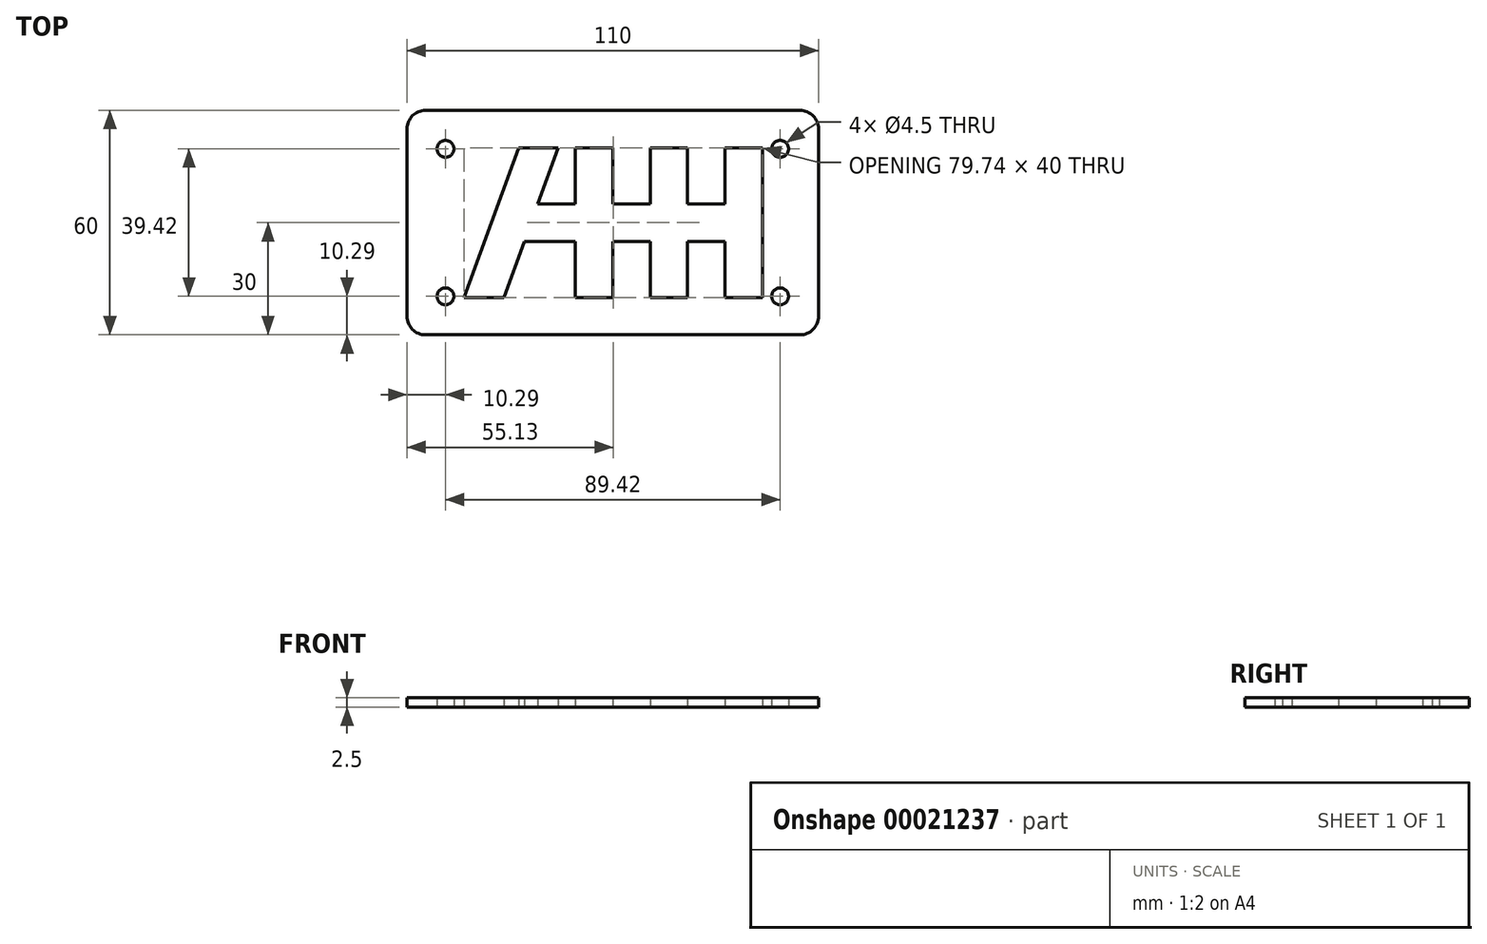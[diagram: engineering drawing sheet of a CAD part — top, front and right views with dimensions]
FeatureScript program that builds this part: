
annotation { "Feature Type Name" : "Feature", "Feature Type Description" : "" }
export const myFeature = defineFeature(function(context is Context, id is Id, definition is map)
    precondition{}
    {
        {
            var Q0;
            Q0=qCreatedBy(makeId("Top.planeOp"),FACE);
            var sketch = newSketch(context, id + "F0", { "sketchPlane" : qUnion([Q0])});
            skLineSegment(sketch, "E0.rect.bottom", {"start": v(50, -30) * mm, "end": v(-50, -30) * mm});
            skLineSegment(sketch, "E0.rect.top", {"start": v(50, 30) * mm, "end": v(-50, 30) * mm});
            skLineSegment(sketch, "E0.rect.left", {"start": v(55, -25) * mm, "end": v(55, 25) * mm});
            skLineSegment(sketch, "E0.rect.right", {"start": v(-55, -25) * mm, "end": v(-55, 25) * mm});
            skPoint(sketch, "E0.rect.middle", {"position": v(0, 0) * mm});
            skPoint(sketch, "E1.visualSharp", {"position": v(-55, 30) * mm});
            skArc(sketch, "E1.filletArc", {"start": v(-50, 30) * mm, "mid": v(-53.54, 28.54) * mm, "end": v(-55, 25) * mm});
            skPoint(sketch, "E2.visualSharp", {"position": v(55, 30) * mm});
            skArc(sketch, "E2.filletArc", {"start": v(55, 25) * mm, "mid": v(53.54, 28.54) * mm, "end": v(50, 30) * mm});
            skPoint(sketch, "E3.visualSharp", {"position": v(55, -30) * mm});
            skArc(sketch, "E3.filletArc", {"start": v(50, -30) * mm, "mid": v(53.54, -28.54) * mm, "end": v(55, -25) * mm});
            skPoint(sketch, "E4.visualSharp", {"position": v(-55, -30) * mm});
            skArc(sketch, "E4.filletArc", {"start": v(-55, -25) * mm, "mid": v(-53.54, -28.54) * mm, "end": v(-50, -30) * mm});
            skLineSegment(sketch, "E5", {"start": v(0, 30) * mm, "end": v(0, -30) * mm, "construction": true});
            skLineSegment(sketch, "E6", {"start": v(-55, 0) * mm, "end": v(55, 0) * mm, "construction": true});
            skCircle(sketch, "E7", {"center": v(-44.7, 19.7) * mm, "radius": 2.25 * mm});
            skCircle(sketch, "E8.MirrorC", {"center": v(44.7, 19.7) * mm, "radius": 2.25 * mm});
            skCircle(sketch, "E9.MirrorC", {"center": v(-44.7, -19.7) * mm, "radius": 2.25 * mm});
            skCircle(sketch, "E10.MirrorC", {"center": v(44.7, -19.7) * mm, "radius": 2.25 * mm});
            skLineSegment(sketch, "E11", {"start": v(-10, 20) * mm, "end": v(0, 20) * mm});
            skLineSegment(sketch, "E12", {"start": v(0, 20) * mm, "end": v(0, 5) * mm});
            skLineSegment(sketch, "E13", {"start": v(0, 5) * mm, "end": v(10, 5) * mm});
            skLineSegment(sketch, "E14", {"start": v(10, 5) * mm, "end": v(10, 20) * mm});
            skLineSegment(sketch, "E15", {"start": v(10, 20) * mm, "end": v(20, 20) * mm});
            skLineSegment(sketch, "E16", {"start": v(20, 20) * mm, "end": v(20, 5) * mm});
            skLineSegment(sketch, "E17", {"start": v(20, 5) * mm, "end": v(30, 5) * mm});
            skLineSegment(sketch, "E18", {"start": v(30, 5) * mm, "end": v(30, 20) * mm});
            skLineSegment(sketch, "E19", {"start": v(30, 20) * mm, "end": v(40, 20) * mm});
            skLineSegment(sketch, "E20", {"start": v(40, 20) * mm, "end": v(40, -20) * mm});
            skLineSegment(sketch, "E21", {"start": v(40, -20) * mm, "end": v(30, -20) * mm});
            skLineSegment(sketch, "E22", {"start": v(30, -20) * mm, "end": v(30, -5) * mm});
            skLineSegment(sketch, "E23", {"start": v(30, -5) * mm, "end": v(20, -5) * mm});
            skLineSegment(sketch, "E24", {"start": v(20, -5) * mm, "end": v(20, -20) * mm});
            skLineSegment(sketch, "E25", {"start": v(20, -20) * mm, "end": v(10, -20) * mm});
            skLineSegment(sketch, "E26", {"start": v(10, -20) * mm, "end": v(10, -5) * mm});
            skLineSegment(sketch, "E27", {"start": v(10, -5) * mm, "end": v(0, -5) * mm});
            skLineSegment(sketch, "E28", {"start": v(0, -5) * mm, "end": v(0, -20) * mm});
            skLineSegment(sketch, "E29", {"start": v(0, -20) * mm, "end": v(-10, -20) * mm});
            skLineSegment(sketch, "E30", {"start": v(-25.18, 20) * mm, "end": v(-39.74, -20) * mm});
            skLineSegment(sketch, "E31", {"start": v(-39.74, -20) * mm, "end": v(-29.1, -20) * mm});
            skLineSegment(sketch, "E32", {"start": v(-29.1, -20) * mm, "end": v(-23.64, -5) * mm});
            skLineSegment(sketch, "E33", {"start": v(-23.64, -5) * mm, "end": v(-10, -5) * mm});
            skLineSegment(sketch, "E34", {"start": v(-10, -5) * mm, "end": v(-10, -20) * mm});
            skLineSegment(sketch, "E35", {"start": v(-10, 20) * mm, "end": v(-10, 5) * mm});
            skLineSegment(sketch, "E36", {"start": v(-10, 5) * mm, "end": v(-20, 5) * mm});
            skLineSegment(sketch, "E37", {"start": v(-20, 5) * mm, "end": v(-14.54, 20) * mm});
            skLineSegment(sketch, "E38", {"start": v(-14.54, 20) * mm, "end": v(-25.18, 20) * mm});
            skLineSegment(sketch, "E39", {"start": v(-20, 5) * mm, "end": v(-29.4, 8.42) * mm, "construction": true});
            skLineSegment(sketch, "E40", {"start": v(-29.1, -20) * mm, "end": v(-14.54, 20) * mm, "construction": true});
            skLineSegment(sketch, "E41", {"start": v(0, 5) * mm, "end": v(0, -5) * mm, "construction": true});
            skLineSegment(sketch, "E42", {"start": v(-44.7, -19.7) * mm, "end": v(-44.7, -30) * mm, "construction": true});
            skLineSegment(sketch, "E43", {"start": v(-44.7, -19.7) * mm, "end": v(-55, -19.71) * mm, "construction": true});
            skSolve(sketch);
        }
        {
            var Q0;
            Q0=makeQuery(id+"F0.imprint","IMPRINT",FACE,{"disambiguationData":[TD([[makeQuery(id+"F0.imprint","IMPRINT",EDGE,{"derivedFrom":sQuery(id+"F0.wireOp",EDGE,"E0.rect.bottom")}),-1.0]])]});
            extrude(context, id + "F1", {"entities" : qUnion([Q0]), "depth" : 2.5 * mm});
        }
    });
